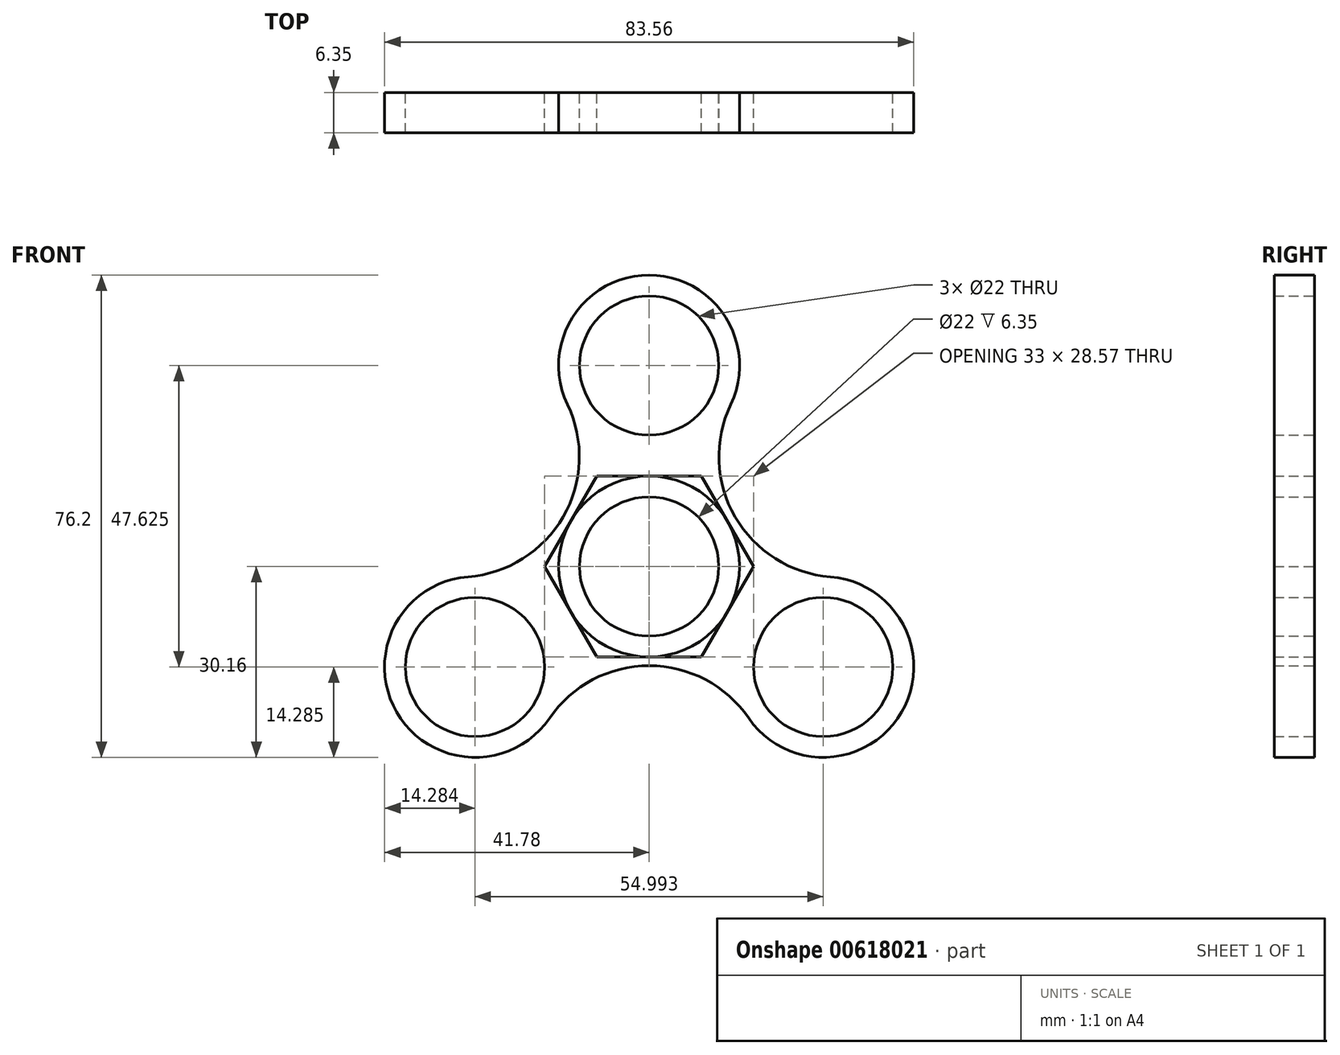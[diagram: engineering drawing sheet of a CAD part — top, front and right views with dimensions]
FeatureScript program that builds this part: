
annotation { "Feature Type Name" : "Feature", "Feature Type Description" : "" }
export const myFeature = defineFeature(function(context is Context, id is Id, definition is map)
    precondition{}
    {
        {
            var Q0;
            Q0=qCreatedBy(makeId("Front.planeOp"),FACE);
            var sketch = newSketch(context, id + "F0", { "sketchPlane" : qUnion([Q0])});
            skCircle(sketch, "E0", {"center": v(0, 0) * mm, "radius": 14.29 * mm});
            skCircle(sketch, "E1", {"center": v(0, 0) * mm, "radius": 11 * mm});
            skCircle(sketch, "E2", {"center": v(0, 31.75) * mm, "radius": 14.29 * mm});
            skCircle(sketch, "E3", {"center": v(0, 31.75) * mm, "radius": 11 * mm});
            skCircle(sketch, "E4.1.0", {"center": v(-27.5, -15.88) * mm, "radius": 11 * mm});
            skCircle(sketch, "E4.1.1", {"center": v(-27.5, -15.88) * mm, "radius": 14.29 * mm});
            skCircle(sketch, "E4.2.0", {"center": v(27.5, -15.88) * mm, "radius": 11 * mm});
            skCircle(sketch, "E4.2.1", {"center": v(27.5, -15.88) * mm, "radius": 14.29 * mm});
            skArc(sketch, "E5", {"start": v(-28.6, -1.63) * mm, "mid": v(-13.58, 7.84) * mm, "end": v(-12.89, 25.58) * mm});
            skArc(sketch, "E6", {"start": v(12.89, 25.58) * mm, "mid": v(13.58, 7.84) * mm, "end": v(28.6, -1.63) * mm});
            skArc(sketch, "E7", {"start": v(15.71, -23.95) * mm, "mid": v(0, -15.68) * mm, "end": v(-15.71, -23.95) * mm});
            skCircle(sketch, "E8.cCircle", {"center": v(0, 0) * mm, "radius": 14.29 * mm, "construction": true});
            skLineSegment(sketch, "E8.0", {"start": v(-8.25, 14.29) * mm, "end": v(8.25, 14.29) * mm});
            skLineSegment(sketch, "E8.1", {"start": v(8.25, 14.29) * mm, "end": v(16.5, 0) * mm});
            skLineSegment(sketch, "E8.2", {"start": v(16.5, 0) * mm, "end": v(8.25, -14.29) * mm});
            skLineSegment(sketch, "E8.3", {"start": v(8.25, -14.29) * mm, "end": v(-8.25, -14.29) * mm});
            skLineSegment(sketch, "E8.4", {"start": v(-8.25, -14.29) * mm, "end": v(-16.5, 0) * mm});
            skLineSegment(sketch, "E8.5", {"start": v(-16.5, 0) * mm, "end": v(-8.25, 14.29) * mm});
            skPoint(sketch, "E8.0.midPoint", {"position": v(0, 14.29) * mm});
            skSolve(sketch);
        }
        {
            var Q0;
            Q0=makeQuery(id+"F0.imprint","IMPRINT",FACE,{"disambiguationData":[TD([[makeQuery(id+"F0.imprint","IMPRINT",EDGE,{"derivedFrom":sQuery(id+"F0.wireOp",EDGE,"E3")}),-1.0]])]});
            var Q1;
            Q1=makeQuery(id+"F0.imprint","IMPRINT",FACE,{"disambiguationData":[TD([[makeQuery(id+"F0.imprint","IMPRINT",EDGE,{"derivedFrom":sQuery(id+"F0.wireOp",EDGE,"E1")}),-1.0]])]});
            var Q2;
            Q2=makeQuery(id+"F0.imprint","IMPRINT",FACE,{"disambiguationData":[TD([[makeQuery(id+"F0.imprint","IMPRINT",EDGE,{"derivedFrom":sQuery(id+"F0.wireOp",EDGE,"E4.1.0")}),-1.0]])]});
            var Q3;
            Q3=makeQuery(id+"F0.imprint","IMPRINT",FACE,{"disambiguationData":[TD([[makeQuery(id+"F0.imprint","IMPRINT",EDGE,{"derivedFrom":sQuery(id+"F0.wireOp",EDGE,"E4.2.0")}),-1.0]])]});
            var Q4;
            {var subQ10=sQuery(id+"F0.wireOp",EDGE,"E5");Q4=makeQuery(id+"F0.imprint","IMPRINT",FACE,{"disambiguationData":[TD([[makeQuery(id+"F0.imprint","IMPRINT",EDGE,{"derivedFrom":subQ10}),-1.0]])]});}
            extrude(context, id + "F1", {"entities" : qUnion([Q0, Q1, Q2, Q3, Q4]), "depth" : 6.35 * mm, "offsetDistance" : 25.4 * mm});
        }
    });
